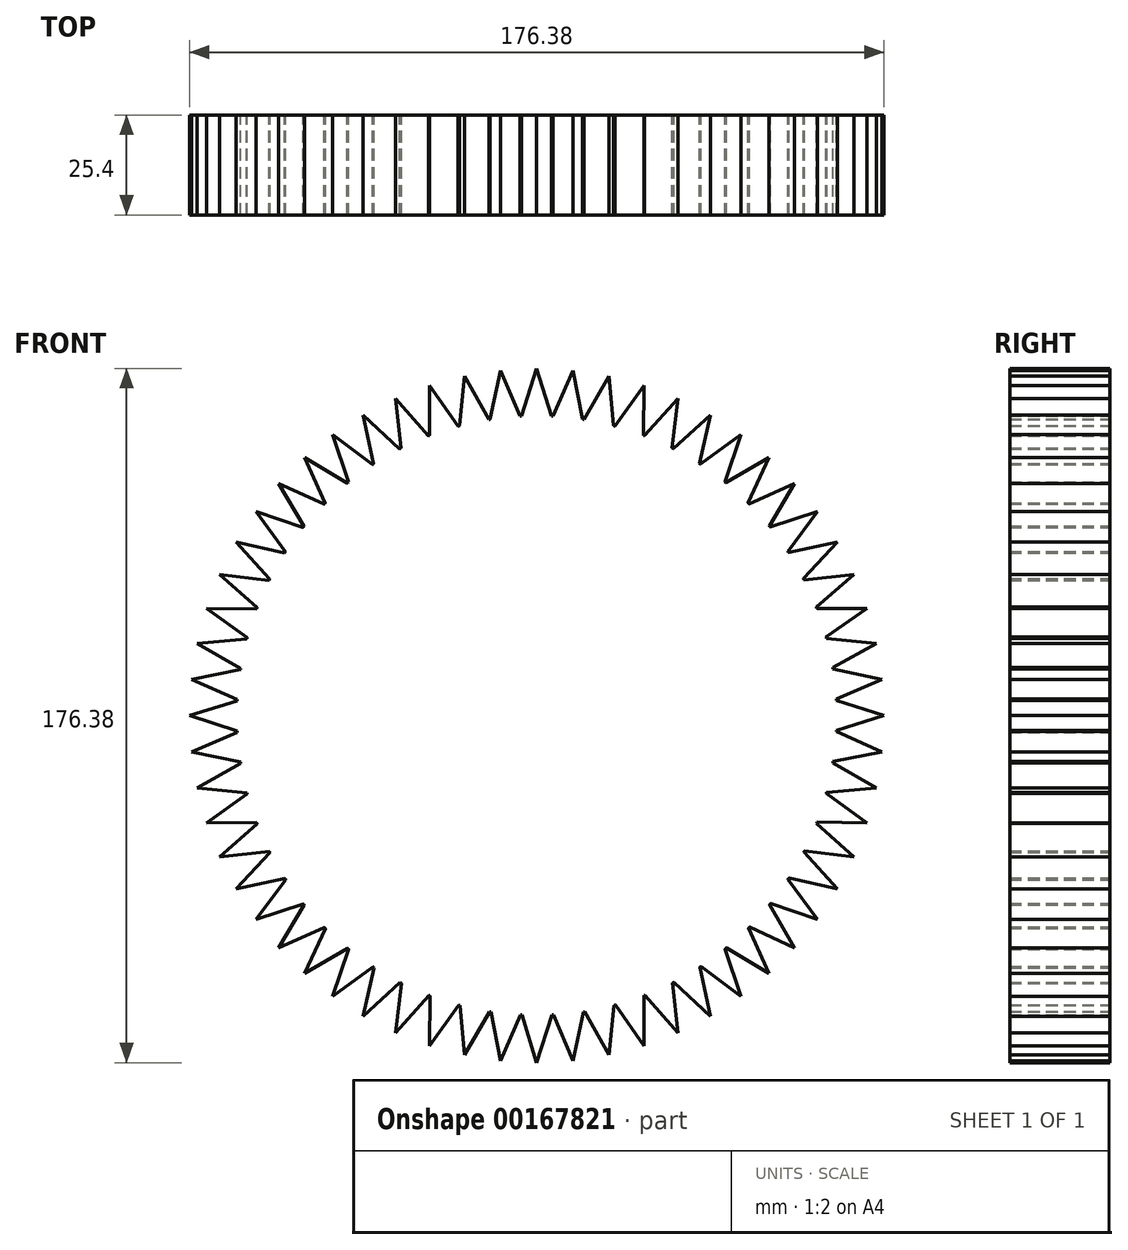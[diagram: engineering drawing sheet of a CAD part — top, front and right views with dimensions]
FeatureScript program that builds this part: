
annotation { "Feature Type Name" : "Feature", "Feature Type Description" : "" }
export const myFeature = defineFeature(function(context is Context, id is Id, definition is map)
    precondition{}
    {
        {
            var Q0;
            Q0=qCreatedBy(makeId("Front.planeOp"),FACE);
            var sketch = newSketch(context, id + "F0", { "sketchPlane" : qUnion([Q0])});
            skCircle(sketch, "E0", {"center": v(0, 0) * mm, "radius": 76.2 * mm});
            skLineSegment(sketch, "E1", {"start": v(-3.89, 76.1) * mm, "end": v(0, 88.2) * mm});
            skLineSegment(sketch, "E2", {"start": v(0, 88.2) * mm, "end": v(3.73, 76.1) * mm});
            skLineSegment(sketch, "E3.1.0", {"start": v(-9.22, 87.7) * mm, "end": v(-4.24, 76.08) * mm});
            skLineSegment(sketch, "E3.1.1", {"start": v(-11.82, 75.28) * mm, "end": v(-9.22, 87.7) * mm});
            skLineSegment(sketch, "E3.2.0", {"start": v(-18.34, 86.26) * mm, "end": v(-12.17, 75.22) * mm});
            skLineSegment(sketch, "E3.2.1", {"start": v(-19.62, 73.63) * mm, "end": v(-18.34, 86.26) * mm});
            skLineSegment(sketch, "E3.3.0", {"start": v(-27.25, 83.87) * mm, "end": v(-19.97, 73.54) * mm});
            skLineSegment(sketch, "E3.3.1", {"start": v(-27.21, 71.17) * mm, "end": v(-27.25, 83.87) * mm});
            skLineSegment(sketch, "E3.4.0", {"start": v(-35.87, 80.57) * mm, "end": v(-27.55, 71.05) * mm});
            skLineSegment(sketch, "E3.4.1", {"start": v(-34.5, 67.94) * mm, "end": v(-35.87, 80.57) * mm});
            skLineSegment(sketch, "E3.5.0", {"start": v(-44.1, 76.38) * mm, "end": v(-34.82, 67.78) * mm});
            skLineSegment(sketch, "E3.5.1", {"start": v(-41.42, 63.96) * mm, "end": v(-44.1, 76.38) * mm});
            skLineSegment(sketch, "E3.6.0", {"start": v(-51.84, 71.35) * mm, "end": v(-41.72, 63.77) * mm});
            skLineSegment(sketch, "E3.6.1", {"start": v(-47.88, 59.28) * mm, "end": v(-51.84, 71.35) * mm});
            skLineSegment(sketch, "E3.7.0", {"start": v(-59.01, 65.54) * mm, "end": v(-48.15, 59.06) * mm});
            skLineSegment(sketch, "E3.7.1", {"start": v(-53.81, 53.95) * mm, "end": v(-59.01, 65.54) * mm});
            skLineSegment(sketch, "E3.8.0", {"start": v(-65.54, 59.01) * mm, "end": v(-54.06, 53.7) * mm});
            skLineSegment(sketch, "E3.8.1", {"start": v(-59.16, 48.03) * mm, "end": v(-65.54, 59.01) * mm});
            skLineSegment(sketch, "E3.9.0", {"start": v(-71.35, 51.84) * mm, "end": v(-59.38, 47.76) * mm});
            skLineSegment(sketch, "E3.9.1", {"start": v(-63.85, 41.59) * mm, "end": v(-71.35, 51.84) * mm});
            skLineSegment(sketch, "E3.10.0", {"start": v(-76.38, 44.1) * mm, "end": v(-64.05, 41.29) * mm});
            skLineSegment(sketch, "E3.10.1", {"start": v(-67.85, 34.68) * mm, "end": v(-76.38, 44.1) * mm});
            skLineSegment(sketch, "E3.11.0", {"start": v(-80.57, 35.87) * mm, "end": v(-68.01, 34.37) * mm});
            skLineSegment(sketch, "E3.11.1", {"start": v(-71.1, 27.4) * mm, "end": v(-80.57, 35.87) * mm});
            skLineSegment(sketch, "E3.12.0", {"start": v(-83.87, 27.25) * mm, "end": v(-71.23, 27.07) * mm});
            skLineSegment(sketch, "E3.12.1", {"start": v(-73.58, 19.82) * mm, "end": v(-83.87, 27.25) * mm});
            skLineSegment(sketch, "E3.13.0", {"start": v(-86.26, 18.34) * mm, "end": v(-73.67, 19.47) * mm});
            skLineSegment(sketch, "E3.13.1", {"start": v(-75.25, 12.02) * mm, "end": v(-86.26, 18.34) * mm});
            skLineSegment(sketch, "E3.14.0", {"start": v(-87.7, 9.22) * mm, "end": v(-75.3, 11.67) * mm});
            skLineSegment(sketch, "E3.14.1", {"start": v(-76.1, 4.09) * mm, "end": v(-87.7, 9.22) * mm});
            skLineSegment(sketch, "E3.15.0", {"start": v(-88.2, 0) * mm, "end": v(-76.1, 3.73) * mm});
            skLineSegment(sketch, "E3.15.1", {"start": v(-76.1, -3.89) * mm, "end": v(-88.2, 0) * mm});
            skLineSegment(sketch, "E3.16.0", {"start": v(-87.7, -9.22) * mm, "end": v(-76.08, -4.24) * mm});
            skLineSegment(sketch, "E3.16.1", {"start": v(-75.28, -11.82) * mm, "end": v(-87.7, -9.22) * mm});
            skLineSegment(sketch, "E3.17.0", {"start": v(-86.26, -18.34) * mm, "end": v(-75.22, -12.17) * mm});
            skLineSegment(sketch, "E3.17.1", {"start": v(-73.63, -19.62) * mm, "end": v(-86.26, -18.34) * mm});
            skLineSegment(sketch, "E3.18.0", {"start": v(-83.87, -27.25) * mm, "end": v(-73.54, -19.97) * mm});
            skLineSegment(sketch, "E3.18.1", {"start": v(-71.17, -27.21) * mm, "end": v(-83.87, -27.25) * mm});
            skLineSegment(sketch, "E3.19.0", {"start": v(-80.57, -35.87) * mm, "end": v(-71.05, -27.55) * mm});
            skLineSegment(sketch, "E3.19.1", {"start": v(-67.94, -34.5) * mm, "end": v(-80.57, -35.87) * mm});
            skLineSegment(sketch, "E3.20.0", {"start": v(-76.38, -44.1) * mm, "end": v(-67.78, -34.82) * mm});
            skLineSegment(sketch, "E3.20.1", {"start": v(-63.96, -41.42) * mm, "end": v(-76.38, -44.1) * mm});
            skLineSegment(sketch, "E3.21.0", {"start": v(-71.35, -51.84) * mm, "end": v(-63.77, -41.72) * mm});
            skLineSegment(sketch, "E3.21.1", {"start": v(-59.28, -47.88) * mm, "end": v(-71.35, -51.84) * mm});
            skLineSegment(sketch, "E3.22.0", {"start": v(-65.54, -59.01) * mm, "end": v(-59.06, -48.15) * mm});
            skLineSegment(sketch, "E3.22.1", {"start": v(-53.95, -53.81) * mm, "end": v(-65.54, -59.01) * mm});
            skLineSegment(sketch, "E3.23.0", {"start": v(-59.01, -65.54) * mm, "end": v(-53.7, -54.06) * mm});
            skLineSegment(sketch, "E3.23.1", {"start": v(-48.03, -59.16) * mm, "end": v(-59.01, -65.54) * mm});
            skLineSegment(sketch, "E3.24.0", {"start": v(-51.84, -71.35) * mm, "end": v(-47.76, -59.38) * mm});
            skLineSegment(sketch, "E3.24.1", {"start": v(-41.59, -63.85) * mm, "end": v(-51.84, -71.35) * mm});
            skLineSegment(sketch, "E3.25.0", {"start": v(-44.1, -76.38) * mm, "end": v(-41.29, -64.05) * mm});
            skLineSegment(sketch, "E3.25.1", {"start": v(-34.68, -67.85) * mm, "end": v(-44.1, -76.38) * mm});
            skLineSegment(sketch, "E3.26.0", {"start": v(-35.87, -80.57) * mm, "end": v(-34.37, -68.01) * mm});
            skLineSegment(sketch, "E3.26.1", {"start": v(-27.4, -71.1) * mm, "end": v(-35.87, -80.57) * mm});
            skLineSegment(sketch, "E3.27.0", {"start": v(-27.25, -83.87) * mm, "end": v(-27.07, -71.23) * mm});
            skLineSegment(sketch, "E3.27.1", {"start": v(-19.82, -73.58) * mm, "end": v(-27.25, -83.87) * mm});
            skLineSegment(sketch, "E3.28.0", {"start": v(-18.34, -86.26) * mm, "end": v(-19.47, -73.67) * mm});
            skLineSegment(sketch, "E3.28.1", {"start": v(-12.02, -75.25) * mm, "end": v(-18.34, -86.26) * mm});
            skLineSegment(sketch, "E3.29.0", {"start": v(-9.22, -87.7) * mm, "end": v(-11.67, -75.3) * mm});
            skLineSegment(sketch, "E3.29.1", {"start": v(-4.09, -76.1) * mm, "end": v(-9.22, -87.7) * mm});
            skLineSegment(sketch, "E3.30.0", {"start": v(0, -88.2) * mm, "end": v(-3.73, -76.1) * mm});
            skLineSegment(sketch, "E3.30.1", {"start": v(3.89, -76.1) * mm, "end": v(0, -88.2) * mm});
            skLineSegment(sketch, "E3.31.0", {"start": v(9.22, -87.7) * mm, "end": v(4.24, -76.08) * mm});
            skLineSegment(sketch, "E3.31.1", {"start": v(11.82, -75.28) * mm, "end": v(9.22, -87.7) * mm});
            skLineSegment(sketch, "E3.32.0", {"start": v(18.34, -86.26) * mm, "end": v(12.17, -75.22) * mm});
            skLineSegment(sketch, "E3.32.1", {"start": v(19.62, -73.63) * mm, "end": v(18.34, -86.26) * mm});
            skLineSegment(sketch, "E3.33.0", {"start": v(27.25, -83.87) * mm, "end": v(19.97, -73.54) * mm});
            skLineSegment(sketch, "E3.33.1", {"start": v(27.21, -71.17) * mm, "end": v(27.25, -83.87) * mm});
            skLineSegment(sketch, "E3.34.0", {"start": v(35.87, -80.57) * mm, "end": v(27.55, -71.05) * mm});
            skLineSegment(sketch, "E3.34.1", {"start": v(34.5, -67.94) * mm, "end": v(35.87, -80.57) * mm});
            skLineSegment(sketch, "E3.35.0", {"start": v(44.1, -76.38) * mm, "end": v(34.82, -67.78) * mm});
            skLineSegment(sketch, "E3.35.1", {"start": v(41.42, -63.96) * mm, "end": v(44.1, -76.38) * mm});
            skLineSegment(sketch, "E3.36.0", {"start": v(51.84, -71.35) * mm, "end": v(41.72, -63.77) * mm});
            skLineSegment(sketch, "E3.36.1", {"start": v(47.88, -59.28) * mm, "end": v(51.84, -71.35) * mm});
            skLineSegment(sketch, "E3.37.0", {"start": v(59.01, -65.54) * mm, "end": v(48.15, -59.06) * mm});
            skLineSegment(sketch, "E3.37.1", {"start": v(53.81, -53.95) * mm, "end": v(59.01, -65.54) * mm});
            skLineSegment(sketch, "E3.38.0", {"start": v(65.54, -59.01) * mm, "end": v(54.06, -53.7) * mm});
            skLineSegment(sketch, "E3.38.1", {"start": v(59.16, -48.03) * mm, "end": v(65.54, -59.01) * mm});
            skLineSegment(sketch, "E3.39.0", {"start": v(71.35, -51.84) * mm, "end": v(59.38, -47.76) * mm});
            skLineSegment(sketch, "E3.39.1", {"start": v(63.85, -41.59) * mm, "end": v(71.35, -51.84) * mm});
            skLineSegment(sketch, "E3.40.0", {"start": v(76.38, -44.1) * mm, "end": v(64.05, -41.29) * mm});
            skLineSegment(sketch, "E3.40.1", {"start": v(67.85, -34.68) * mm, "end": v(76.38, -44.1) * mm});
            skLineSegment(sketch, "E3.41.0", {"start": v(80.57, -35.87) * mm, "end": v(68.01, -34.37) * mm});
            skLineSegment(sketch, "E3.41.1", {"start": v(71.1, -27.4) * mm, "end": v(80.57, -35.87) * mm});
            skLineSegment(sketch, "E3.42.0", {"start": v(83.87, -27.25) * mm, "end": v(71.23, -27.07) * mm});
            skLineSegment(sketch, "E3.42.1", {"start": v(73.58, -19.82) * mm, "end": v(83.87, -27.25) * mm});
            skLineSegment(sketch, "E3.43.0", {"start": v(86.26, -18.34) * mm, "end": v(73.67, -19.47) * mm});
            skLineSegment(sketch, "E3.43.1", {"start": v(75.25, -12.02) * mm, "end": v(86.26, -18.34) * mm});
            skLineSegment(sketch, "E3.44.0", {"start": v(87.7, -9.22) * mm, "end": v(75.3, -11.67) * mm});
            skLineSegment(sketch, "E3.44.1", {"start": v(76.1, -4.09) * mm, "end": v(87.7, -9.22) * mm});
            skLineSegment(sketch, "E3.45.0", {"start": v(88.2, 0) * mm, "end": v(76.1, -3.73) * mm});
            skLineSegment(sketch, "E3.45.1", {"start": v(76.1, 3.89) * mm, "end": v(88.2, 0) * mm});
            skLineSegment(sketch, "E3.46.0", {"start": v(87.7, 9.22) * mm, "end": v(76.08, 4.24) * mm});
            skLineSegment(sketch, "E3.46.1", {"start": v(75.28, 11.82) * mm, "end": v(87.7, 9.22) * mm});
            skLineSegment(sketch, "E3.47.0", {"start": v(86.26, 18.34) * mm, "end": v(75.22, 12.17) * mm});
            skLineSegment(sketch, "E3.47.1", {"start": v(73.63, 19.62) * mm, "end": v(86.26, 18.34) * mm});
            skLineSegment(sketch, "E3.48.0", {"start": v(83.87, 27.25) * mm, "end": v(73.54, 19.97) * mm});
            skLineSegment(sketch, "E3.48.1", {"start": v(71.17, 27.21) * mm, "end": v(83.87, 27.25) * mm});
            skLineSegment(sketch, "E3.49.0", {"start": v(80.57, 35.87) * mm, "end": v(71.05, 27.55) * mm});
            skLineSegment(sketch, "E3.49.1", {"start": v(67.94, 34.5) * mm, "end": v(80.57, 35.87) * mm});
            skLineSegment(sketch, "E3.50.0", {"start": v(76.38, 44.1) * mm, "end": v(67.78, 34.82) * mm});
            skLineSegment(sketch, "E3.50.1", {"start": v(63.96, 41.42) * mm, "end": v(76.38, 44.1) * mm});
            skLineSegment(sketch, "E3.51.0", {"start": v(71.35, 51.84) * mm, "end": v(63.77, 41.72) * mm});
            skLineSegment(sketch, "E3.51.1", {"start": v(59.28, 47.88) * mm, "end": v(71.35, 51.84) * mm});
            skLineSegment(sketch, "E3.52.0", {"start": v(65.54, 59.01) * mm, "end": v(59.06, 48.15) * mm});
            skLineSegment(sketch, "E3.52.1", {"start": v(53.95, 53.81) * mm, "end": v(65.54, 59.01) * mm});
            skLineSegment(sketch, "E3.53.0", {"start": v(59.01, 65.54) * mm, "end": v(53.7, 54.06) * mm});
            skLineSegment(sketch, "E3.53.1", {"start": v(48.03, 59.16) * mm, "end": v(59.01, 65.54) * mm});
            skLineSegment(sketch, "E3.54.0", {"start": v(51.84, 71.35) * mm, "end": v(47.76, 59.38) * mm});
            skLineSegment(sketch, "E3.54.1", {"start": v(41.59, 63.85) * mm, "end": v(51.84, 71.35) * mm});
            skLineSegment(sketch, "E3.55.0", {"start": v(44.1, 76.38) * mm, "end": v(41.29, 64.05) * mm});
            skLineSegment(sketch, "E3.55.1", {"start": v(34.68, 67.85) * mm, "end": v(44.1, 76.38) * mm});
            skLineSegment(sketch, "E3.56.0", {"start": v(35.87, 80.57) * mm, "end": v(34.37, 68.01) * mm});
            skLineSegment(sketch, "E3.56.1", {"start": v(27.4, 71.1) * mm, "end": v(35.87, 80.57) * mm});
            skLineSegment(sketch, "E3.57.0", {"start": v(27.25, 83.87) * mm, "end": v(27.07, 71.23) * mm});
            skLineSegment(sketch, "E3.57.1", {"start": v(19.82, 73.58) * mm, "end": v(27.25, 83.87) * mm});
            skLineSegment(sketch, "E3.58.0", {"start": v(18.34, 86.26) * mm, "end": v(19.47, 73.67) * mm});
            skLineSegment(sketch, "E3.58.1", {"start": v(12.02, 75.25) * mm, "end": v(18.34, 86.26) * mm});
            skLineSegment(sketch, "E3.59.0", {"start": v(9.22, 87.7) * mm, "end": v(11.67, 75.3) * mm});
            skLineSegment(sketch, "E3.59.1", {"start": v(4.09, 76.1) * mm, "end": v(9.22, 87.7) * mm});
            skSolve(sketch);
        }
        {
            var Q0;
            Q0 = qSketchRegion(id + "F0", true);
            extrude(context, id + "F1", {"entities" : qUnion([Q0]), "endBound" : BoundingType.SYMMETRIC, "depth" : 25.4 * mm});
        }
    });
